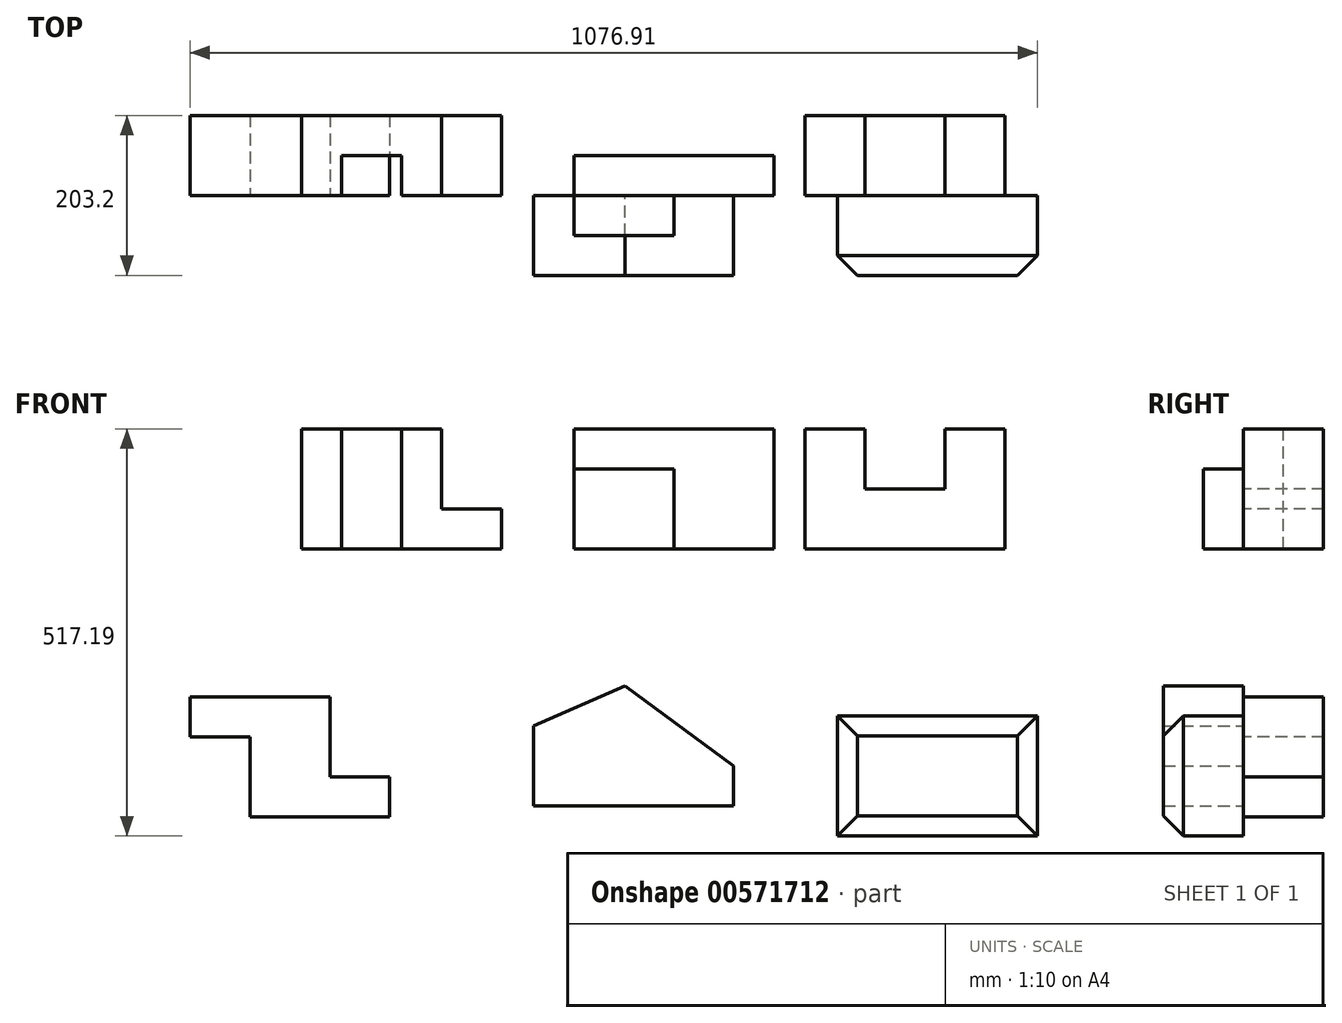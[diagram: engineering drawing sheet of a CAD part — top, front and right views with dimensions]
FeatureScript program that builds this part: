
annotation { "Feature Type Name" : "Feature", "Feature Type Description" : "" }
export const myFeature = defineFeature(function(context is Context, id is Id, definition is map)
    precondition{}
    {
        {
            var Q0;
            Q0=qCreatedBy(makeId("Front.planeOp"),FACE);
            var sketch = newSketch(context, id + "F0", { "sketchPlane" : qUnion([Q0])});
            skLineSegment(sketch, "E0", {"start": v(0, 0) * mm, "end": v(254, 0) * mm});
            skLineSegment(sketch, "E1", {"start": v(254, 0) * mm, "end": v(254, 152.4) * mm});
            skLineSegment(sketch, "E2", {"start": v(254, 152.4) * mm, "end": v(177.8, 152.4) * mm});
            skLineSegment(sketch, "E3", {"start": v(177.8, 152.4) * mm, "end": v(177.8, 76.2) * mm});
            skLineSegment(sketch, "E4", {"start": v(177.8, 76.2) * mm, "end": v(76.2, 76.2) * mm});
            skLineSegment(sketch, "E5", {"start": v(76.2, 76.2) * mm, "end": v(76.2, 152.4) * mm});
            skLineSegment(sketch, "E6", {"start": v(76.2, 152.4) * mm, "end": v(0, 152.4) * mm});
            skLineSegment(sketch, "E7", {"start": v(0, 152.4) * mm, "end": v(0, 0) * mm});
            skSolve(sketch);
        }
        {
            var Q0;
            Q0=makeQuery(id+"F0.imprint","IMPRINT",FACE,{"disambiguationData":[TD([[makeQuery(id+"F0.imprint","IMPRINT",EDGE,{"derivedFrom":sQuery(id+"F0.wireOp",EDGE,"E0")}),1.0]])]});
            extrude(context, id + "F1", {"entities" : qUnion([Q0]), "oppositeDirection" : true, "depth" : 101.6 * mm, "offsetDistance" : 25.4 * mm});
        }
        {
            var Q0;
            Q0=qCreatedBy(makeId("Front.planeOp"),FACE);
            var sketch = newSketch(context, id + "F2", { "sketchPlane" : qUnion([Q0])});
            skLineSegment(sketch, "E8", {"start": v(-114.02, 0) * mm, "end": v(-293.71, 0) * mm});
            skLineSegment(sketch, "E9", {"start": v(-293.71, 0) * mm, "end": v(-293.71, 101.6) * mm});
            skLineSegment(sketch, "E10", {"start": v(-293.71, 101.6) * mm, "end": v(-166.71, 101.6) * mm});
            skLineSegment(sketch, "E11", {"start": v(-166.71, 101.6) * mm, "end": v(-166.71, 0) * mm});
            skLineSegment(sketch, "E12", {"start": v(-293.71, 101.6) * mm, "end": v(-293.71, 152.4) * mm});
            skLineSegment(sketch, "E13", {"start": v(-293.71, 152.4) * mm, "end": v(-39.71, 152.4) * mm});
            skLineSegment(sketch, "E14", {"start": v(-39.71, 152.4) * mm, "end": v(-39.71, 0) * mm});
            skLineSegment(sketch, "E15", {"start": v(-39.71, 0) * mm, "end": v(-166.71, 0) * mm});
            skSolve(sketch);
        }
        {
            var Q0;
            Q0=makeQuery(id+"F2.imprint","IMPRINT",FACE,{"disambiguationData":[TD([[makeQuery(id+"F2.imprint","IMPRINT",EDGE,{"derivedFrom":sQuery(id+"F2.wireOp",EDGE,"E10")}),1.0]])]});
            var Q1;
            Q1=makeQuery(id+"F2.imprint","IMPRINT",FACE,{"disambiguationData":[TD([[makeQuery(id+"F2.imprint","IMPRINT",EDGE,{"derivedFrom":sQuery(id+"F2.wireOp",EDGE,"E8")}),-1.0]])]});
            extrude(context, id + "F3", {"entities" : qUnion([Q0, Q1]), "oppositeDirection" : true, "depth" : 50.8 * mm, "offsetDistance" : 25.4 * mm});
        }
        {
            var Q0;
            Q0=makeQuery(id+"F3.opExtrude","CAP_FACE",FACE,{"disambiguationData":[OSD([sQuery(id+"F2.wireOp",EDGE,"E8"),sQuery(id+"F2.wireOp",EDGE,"E9"),sQuery(id+"F2.wireOp",EDGE,"E12"),sQuery(id+"F2.wireOp",EDGE,"E13"),sQuery(id+"F2.wireOp",EDGE,"E14"),sQuery(id+"F2.wireOp",EDGE,"E15")])],"isStart":true});
            var sketch = newSketch(context, id + "F4", { "sketchPlane" : qUnion([Q0])});
            skPoint(sketch, "E16.endSnap0", {"position": v(-166.71, 0) * mm});
            skLineSegment(sketch, "E17.bottom", {"start": v(-293.71, 0) * mm, "end": v(-166.71, 0) * mm});
            skLineSegment(sketch, "E17.top", {"start": v(-293.71, 101.6) * mm, "end": v(-166.71, 101.6) * mm});
            skLineSegment(sketch, "E17.left", {"start": v(-293.71, 0) * mm, "end": v(-293.71, 101.6) * mm});
            skLineSegment(sketch, "E17.right", {"start": v(-166.71, 0) * mm, "end": v(-166.71, 101.6) * mm});
            skSolve(sketch);
        }
        {
            var Q0;
            Q0=makeQuery(id+"F4.imprint","IMPRINT",FACE,{"disambiguationData":[TD([[makeQuery(id+"F4.imprint","IMPRINT",EDGE,{"derivedFrom":sQuery(id+"F4.wireOp",EDGE,"E17.bottom")}),-1.0]])]});
            extrude(context, id + "F5", {"entities" : qUnion([Q0]), "operationType" : NewBodyOperationType.ADD, "depth" : 50.8 * mm, "offsetDistance" : 25.4 * mm});
        }
        {
            var Q0;
            Q0=qCreatedBy(makeId("Front.planeOp"),FACE);
            var sketch = newSketch(context, id + "F6", { "sketchPlane" : qUnion([Q0])});
            skLineSegment(sketch, "E18", {"start": v(-639.62, 0) * mm, "end": v(-639.62, 152.4) * mm});
            skLineSegment(sketch, "E19", {"start": v(-639.62, 152.4) * mm, "end": v(-461.82, 152.4) * mm});
            skLineSegment(sketch, "E20", {"start": v(-385.62, 50.8) * mm, "end": v(-385.62, 0) * mm});
            skLineSegment(sketch, "E21", {"start": v(-385.62, 0) * mm, "end": v(-639.62, 0) * mm});
            skLineSegment(sketch, "E22", {"start": v(-461.82, 152.4) * mm, "end": v(-461.82, 50.8) * mm});
            skLineSegment(sketch, "E23", {"start": v(-461.82, 50.8) * mm, "end": v(-385.62, 50.8) * mm});
            skSolve(sketch);
        }
        {
            var Q0;
            Q0=makeQuery(id+"F6.imprint","IMPRINT",FACE,{"disambiguationData":[TD([[makeQuery(id+"F6.imprint","IMPRINT",EDGE,{"derivedFrom":sQuery(id+"F6.wireOp",EDGE,"E18")}),-1.0]])]});
            extrude(context, id + "F7", {"entities" : qUnion([Q0]), "oppositeDirection" : true, "depth" : 101.6 * mm, "offsetDistance" : 25.4 * mm});
        }
        {
            var Q0;
            Q0=makeQuery(id+"F7.opExtrude","SWEPT_FACE",FACE,{"disambiguationData":[OSD([sQuery(id+"F6.wireOp",EDGE,"E19")])]});
            var sketch = newSketch(context, id + "F8", { "sketchPlane" : qUnion([Q0])});
            skLineSegment(sketch, "E24", {"start": v(-588.82, 0) * mm, "end": v(-588.82, 50.8) * mm});
            skLineSegment(sketch, "E25", {"start": v(-588.82, 50.8) * mm, "end": v(-512.62, 50.8) * mm});
            skLineSegment(sketch, "E26", {"start": v(-512.62, 50.8) * mm, "end": v(-512.62, 0) * mm});
            skSolve(sketch);
        }
        {
            var Q0;
            Q0 = qSketchRegion(id + "F8", true);
            var Q1;
            {var subQ0=sQuery(id+"F8.wireOp",EDGE,"E24");Q1=makeQuery(id+"F8.imprint","IMPRINT",FACE,{"disambiguationData":[TD([[makeQuery(id+"F8.imprint","IMPRINT",EDGE,{"derivedFrom":subQ0}),-1.0]])]});}
            extrude(context, id + "F9", {"entities" : qUnion([Q0, Q1]), "operationType" : NewBodyOperationType.REMOVE, "oppositeDirection" : true, "depth" : 152.4 * mm, "offsetDistance" : 25.4 * mm});
        }
        {
            var Q0;
            Q0=qCreatedBy(makeId("Front.planeOp"),FACE);
            var sketch = newSketch(context, id + "F10", { "sketchPlane" : qUnion([Q0])});
            skLineSegment(sketch, "E27", {"start": v(-781.6, -188.1) * mm, "end": v(-603.8, -188.1) * mm});
            skLineSegment(sketch, "E28", {"start": v(-603.8, -188.1) * mm, "end": v(-603.8, -289.7) * mm});
            skLineSegment(sketch, "E29", {"start": v(-603.8, -289.7) * mm, "end": v(-527.6, -289.7) * mm});
            skLineSegment(sketch, "E30", {"start": v(-527.6, -289.7) * mm, "end": v(-527.6, -340.5) * mm});
            skLineSegment(sketch, "E31", {"start": v(-527.6, -340.5) * mm, "end": v(-705.4, -340.5) * mm});
            skLineSegment(sketch, "E32", {"start": v(-705.4, -340.5) * mm, "end": v(-705.4, -238.9) * mm});
            skLineSegment(sketch, "E33", {"start": v(-705.4, -238.9) * mm, "end": v(-781.6, -238.9) * mm});
            skLineSegment(sketch, "E34", {"start": v(-781.6, -238.9) * mm, "end": v(-781.6, -188.1) * mm});
            skSolve(sketch);
        }
        {
            var Q0;
            Q0=makeQuery(id+"F10.imprint","IMPRINT",FACE,{"disambiguationData":[TD([[makeQuery(id+"F10.imprint","IMPRINT",EDGE,{"derivedFrom":sQuery(id+"F10.wireOp",EDGE,"E27")}),-1.0]])]});
            extrude(context, id + "F11", {"entities" : qUnion([Q0]), "oppositeDirection" : true, "depth" : 101.6 * mm, "offsetDistance" : 25.4 * mm});
        }
        {
            var Q0;
            Q0=qCreatedBy(makeId("Front.planeOp"),FACE);
            var sketch = newSketch(context, id + "F12", { "sketchPlane" : qUnion([Q0])});
            skLineSegment(sketch, "E35", {"start": v(-345.33, -326.59) * mm, "end": v(-345.33, -224.99) * mm});
            skLineSegment(sketch, "E36", {"start": v(-345.33, -224.99) * mm, "end": v(-228.93, -174.19) * mm});
            skLineSegment(sketch, "E37", {"start": v(-228.93, -174.19) * mm, "end": v(-91.33, -275.79) * mm});
            skLineSegment(sketch, "E38", {"start": v(-91.33, -275.79) * mm, "end": v(-91.33, -326.59) * mm});
            skLineSegment(sketch, "E39", {"start": v(-91.33, -326.59) * mm, "end": v(-345.33, -326.59) * mm});
            skSolve(sketch);
        }
        {
            var Q0;
            Q0 = qSketchRegion(id + "F12", true);
            extrude(context, id + "F13", {"entities" : qUnion([Q0]), "depth" : 101.6 * mm, "offsetDistance" : 25.4 * mm});
        }
        {
            var Q0;
            Q0=qCreatedBy(makeId("Front.planeOp"),FACE);
            var sketch = newSketch(context, id + "F14", { "sketchPlane" : qUnion([Q0])});
            skLineSegment(sketch, "E40", {"start": v(41.32, -212.39) * mm, "end": v(295.32, -212.39) * mm});
            skLineSegment(sketch, "E41", {"start": v(295.32, -212.39) * mm, "end": v(295.32, -364.79) * mm});
            skLineSegment(sketch, "E42", {"start": v(295.32, -364.79) * mm, "end": v(41.32, -364.79) * mm});
            skLineSegment(sketch, "E43", {"start": v(41.32, -212.39) * mm, "end": v(41.32, -364.79) * mm});
            skSolve(sketch);
        }
        {
            var Q0;
            Q0 = qSketchRegion(id + "F14", true);
            extrude(context, id + "F15", {"entities" : qUnion([Q0]), "depth" : 101.6 * mm, "offsetDistance" : 25.4 * mm});
        }
        {
            var Q0;
            Q0=makeQuery(id+"F15.opExtrude","CAP_FACE",FACE,{"disambiguationData":[OSD([sQuery(id+"F14.wireOp",EDGE,"E40"),sQuery(id+"F14.wireOp",EDGE,"E41"),sQuery(id+"F14.wireOp",EDGE,"E42"),sQuery(id+"F14.wireOp",EDGE,"E43")])],"isStart":false});
            chamfer(context, id + "F16", {"entities" : qUnion([Q0]), "width" : 25.4 * mm, "tangentPropagation" : true});
        }
    });
